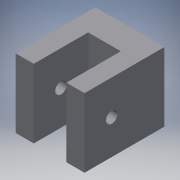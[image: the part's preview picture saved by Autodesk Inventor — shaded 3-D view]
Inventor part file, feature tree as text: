
AUTODESK INVENTOR PART (.ipt)
format: ipt  version: 2019 (Build 230136000, 136)  size: 139,776 bytes
history: native  units: in
note: dims shown in document units (in); Inventor stores cm internally (conversion verified against a paired STEP export)
features: extrude x5, sketch x5, projected_geometry x1
ambient origin geometry x8: Origin, YZ Plane, XZ Plane, XY Plane, X Axis, Y Axis, Z Axis, Center Point
bodies: Solid1 (feature_tree)
feature tree (11):
  extrude  "Extrusion1"  Depth=0.748in
  extrude  "Extrusion2"  Depth=0.3543in
  extrude  "Extrusion3"  Depth=0.5906in
  extrude  "Extrusion4"  Depth=0.5906in
  extrude  "Extrusion5"  Depth=0.126in
  sketch  "Sketch1"  dims[d0=0.748in d1=0.748in]
  sketch  "Sketch2"  dims[d2=0.2756in d3=0.0in d4=0.3543in]
  projected_geometry  "Projected Loop1"
  sketch  "Sketch3"  dims[d5=0.5906in d6=0.0in d7=0.1673in]
  sketch  "Sketch4"  dims[d8=0.5906in d9=0.0in d10=0.124in]
  sketch  "Sketch5"  dims[d11=0.5906in d12=0.0in d13=0.3248in d14=0.126in d15=0.0in]
